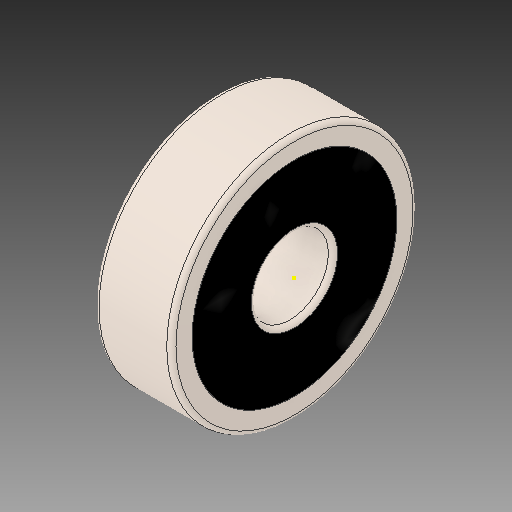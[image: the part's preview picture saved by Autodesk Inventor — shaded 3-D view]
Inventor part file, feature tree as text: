
AUTODESK INVENTOR PART (.ipt)
format: ipt  version: 2018 (Build 220112000, 112)  size: 2,301,952 bytes
history: imported  units: mm
features: other x22, sketch x3, imported_body x1
ambient origin geometry x8: Origin, YZ Plane, XZ Plane, XY Plane, X Axis, Y Axis, Z Axis, Center Point
bodies: Solid1 (imported_parasolid), Solid2 (imported_parasolid), Solid3 (imported_parasolid), Solid4 (imported_parasolid), Solid5 (imported_parasolid), Solid6 (imported_parasolid), Solid7 (imported_parasolid), Solid8 (imported_parasolid), Solid9 (imported_parasolid), Solid10 (imported_parasolid), Solid11 (imported_parasolid), Solid12 (imported_parasolid), Solid13 (imported_parasolid), Solid14 (imported_parasolid), Solid15 (imported_parasolid), Solid16 (imported_parasolid), Solid17 (imported_parasolid), Solid18 (imported_parasolid), Solid19 (imported_parasolid), Solid20 (imported_parasolid)
feature tree (26):
  other  "SKF 625.ipt"
  other  "Solid1::SKF 625.ipt"
  other  "Solid2::SKF 625.ipt"
  other  "Solid3::SKF 625.ipt"
  other  "Solid4::SKF 625.ipt"
  other  "Solid5::SKF 625.ipt"
  other  "Solid6::SKF 625.ipt"
  other  "Solid7::SKF 625.ipt"
  other  "Solid8::SKF 625.ipt"
  other  "Solid9::SKF 625.ipt"
  other  "Solid10::SKF 625.ipt"
  other  "Solid11::SKF 625.ipt"
  other  "Solid12::SKF 625.ipt"
  other  "Solid13::SKF 625.ipt"
  other  "Solid14::SKF 625.ipt"
  other  "Solid15::SKF 625.ipt"
  other  "Solid16::SKF 625.ipt"
  other  "Solid17::SKF 625.ipt"
  other  "Solid18::SKF 625.ipt"
  other  "Solid19::SKF 625.ipt"
  other  "Solid20::SKF 625.ipt"
  other  "TaggingFeature1"
  sketch  "Sketch1"  dims[d0=10.0mm]
  sketch  "Sketch2"
  sketch  "Sketch3"
  imported_body  NMx_Import_Brep_tag  [imported B-rep: ~49 faces, bbox_mm=None]
